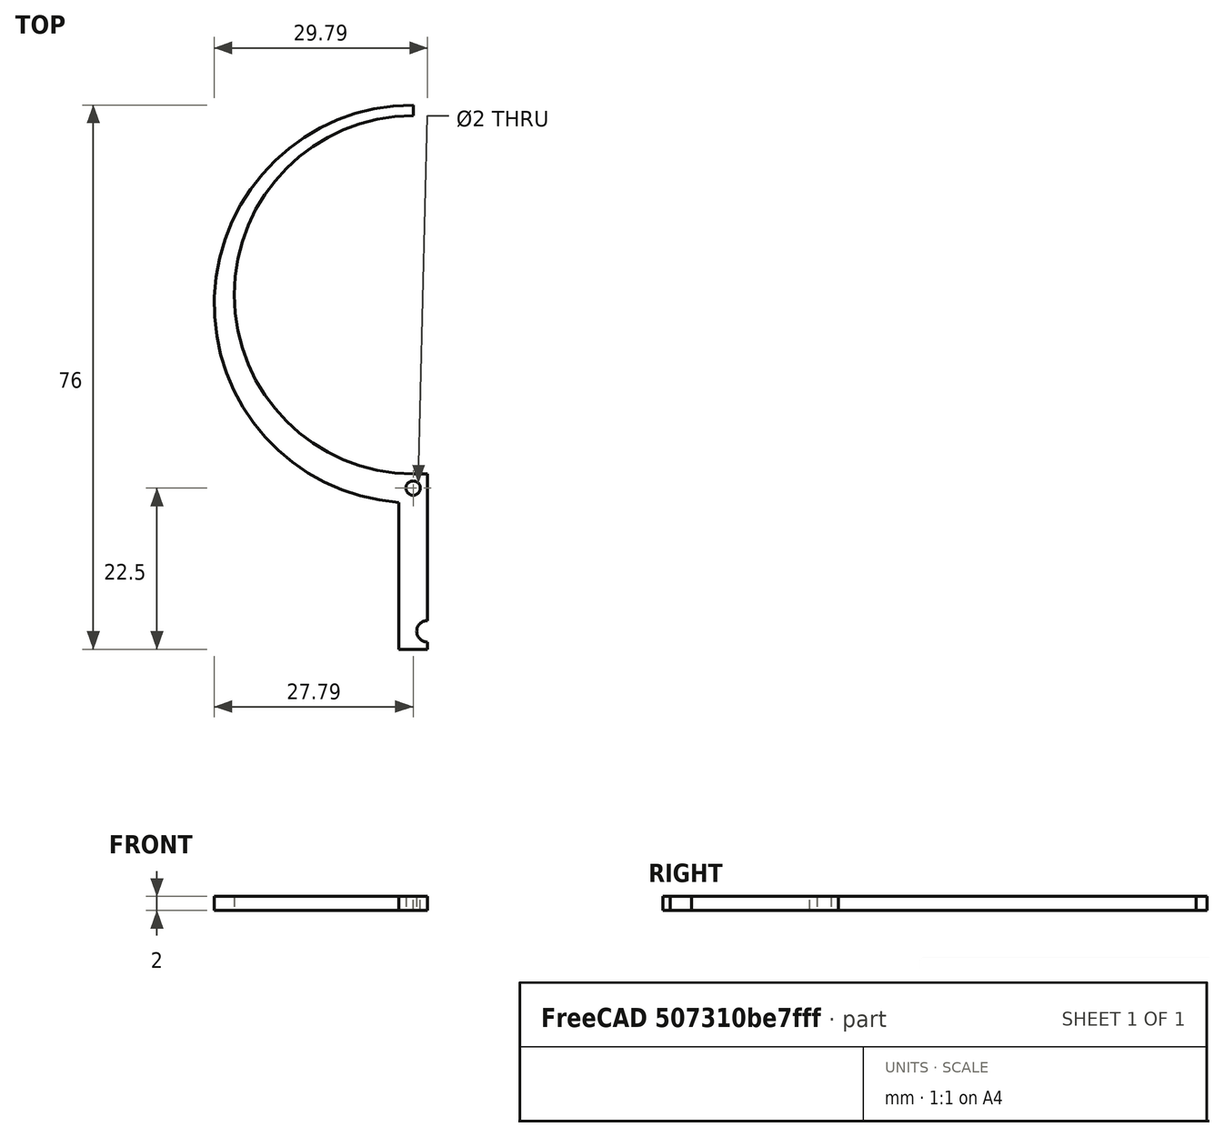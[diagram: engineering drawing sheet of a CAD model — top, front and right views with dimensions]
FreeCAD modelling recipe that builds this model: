
FCSTD DOCUMENT  (FreeCAD 0.16R6414 (Git))
Label: MoveArm
License: All rights reserved
LicenseURL: http://en.wikipedia.org/wiki/All_rights_reserved
objects: Sketcher::SketchObject×1, PartDesign::Pad×1
note: 3 computed .brp shape members not serialized (recipe doc carries the construction recipe); baked Part::Feature solids carry a one-line shape summary decoded from their .brp

FEATURE [Sketcher::SketchObject] Sketch
  sketch-geometry (11):
    g0: ArcOfCircle CenterX=0 CenterY=25 CenterZ=0 NormalX=0 NormalY=0 NormalZ=1 Radius=25 StartAngle=1.5708 EndAngle=4.71239
    g1: Circle CenterX=0 CenterY=-2 CenterZ=0 NormalX=0 NormalY=0 NormalZ=1 Radius=1
    g2: LineSegment StartX=0 StartY=50 StartZ=0 EndX=0 EndY=51.5 EndZ=0
    g3: ArcOfCircle CenterX=0 CenterY=23.714 CenterZ=0 NormalX=0 NormalY=0 NormalZ=1 Radius=27.786 StartAngle=1.5708 EndAngle=4.64035
    g4: LineSegment StartX=-2 StartY=-4 StartZ=0 EndX=-2 EndY=-24.5 EndZ=0
    g5: LineSegment StartX=2 StartY=-20.5 StartZ=0 EndX=2 EndY=0 EndZ=0
    g6: LineSegment StartX=2 StartY=0 StartZ=0 EndX=0 EndY=0 EndZ=0
    g7: ArcOfCircle CenterX=2 CenterY=-22 CenterZ=0 NormalX=0 NormalY=0 NormalZ=1 Radius=1.5 StartAngle=1.5708 EndAngle=4.71239
    g8: LineSegment StartX=2 StartY=-23.5 StartZ=0 EndX=2 EndY=-24.5 EndZ=0
    g9: LineSegment StartX=2 StartY=-24.5 StartZ=0 EndX=-2 EndY=-24.5 EndZ=0
    g10: LineSegment [constr] StartX=2 StartY=-20.5 StartZ=0 EndX=2 EndY=-23.5 EndZ=0
  constraints (35):
    c: PointOnObject(g0,g-2)
    c: PointOnObject(g0,g-2)
    c: PointOnObject(g0,g-2)
    c: Coincident(g0,g-1)
    c: Radius(g0) = 25
    c: PointOnObject(g1,g-2)
    c: Radius(g1) = 1
    c: DistanceY(g-1,g1) = -2
    c: Coincident(g2,g0)
    c: PointOnObject(g2,g-2)
    c: DistanceY(g2) = 1.5
    c: PointOnObject(g3,g-2)
    c: Coincident(g3,g2)
    c: DistanceY(g3,g1) = 2
    c: DistanceX(g3,g1) = 2
    c: Coincident(g4,g3)
    c: Vertical(g4)
    c: PointOnObject(g5,g-1)
    c: Vertical(g5)
    c: Coincident(g6,g5)
    c: Coincident(g6,g-1)
    c: DistanceX(g6) = -2
    c: Coincident(g7,g5)
    c: Radius(g7) = 1.5
    c: Coincident(g8,g7)
    c: Vertical(g8)
    c: Coincident(g8,g9)
    c: Horizontal(g9)
    c: Coincident(g4,g9)
    c: Vertical(g10)
    c: Coincident(g5,g10)
    c: Coincident(g10,g7)
    c: Distance(g8) = 1
    c: DistanceY(g1,g7) = -20
    c: PointOnObject(g7,g10)
FEATURE [PartDesign::Pad] Pad
  Length = 2
  Length2 = 100
  Sketch = -> Sketch
  Type = 0
